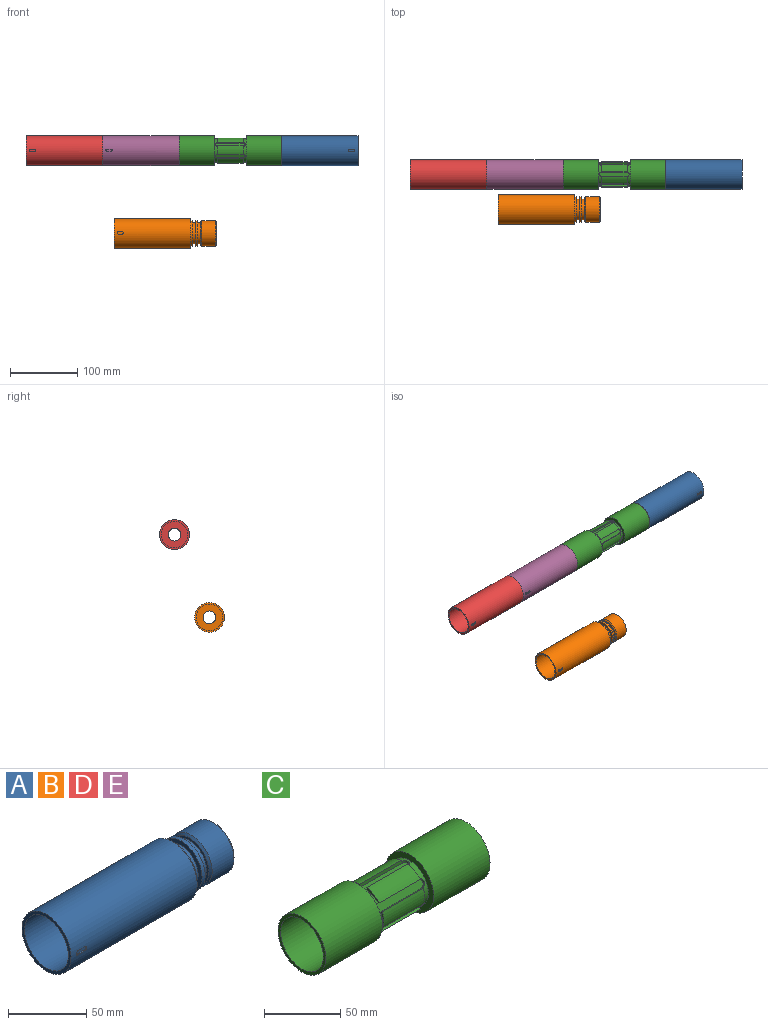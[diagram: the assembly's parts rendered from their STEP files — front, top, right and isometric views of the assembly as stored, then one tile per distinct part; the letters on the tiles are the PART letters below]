
ASSEMBLY  parts=5 mates=4
PART A: 23 faces, bbox 152.4x44.5x44.5 mm
  f0: cylinder r=19.05mm len=38.1mm, axis (1,0,0), area 2371.4mm2, adj f21,f22
  f1: cylinder r=22.23mm len=114.3mm, axis (1,0,0), area 15933.2mm2, adj f2,f8,f9,f10,f11,f12
  f2: plane 44.45x44.45mm, normal (-1,0,0), area 314.7mm2, adj f1,f3
  f3: cylinder r=19.84mm len=44.45mm, axis (1,0,0), area 5542.1mm2, adj f2,f4
  f4: plane 39.69x39.69mm, normal (-1,0,0), area 952.1mm2, adj f3,f5
  f5: cylinder r=9.53mm len=107.95mm, axis (1,0,0), area 6460.5mm2, adj f4,f6
  f6: plane 35.05x35.05mm, normal (1,0,0), area 680mm2, adj f5,f22
  f7: cylinder r=19.05mm len=38.1mm, axis (1,0,0), area 343.5mm2, adj f8,f18
  f8: plane 44.45x44.45mm, normal (1,0,0), area 411.7mm2, adj f1,f7
  f9: plane 6.35x0.96mm, normal (0,0,-1), area 6.1mm2, adj f1,f10,f12,f13
  f10: cylinder r=1.59mm len=3.18mm, axis (0,-1,0), area 4.9mm2, adj f1,f9,f11,f13
  f11: plane 6.35x0.96mm, normal (0,0,1), area 6.1mm2, adj f1,f10,f12,f13
  f12: cylinder r=1.59mm len=3.18mm, axis (0,-1,0), area 4.9mm2, adj f1,f9,f11,f13
  f13: plane 9.53x3.18mm, normal (0,-1,0), area 28.1mm2, adj f9,f10,f11,f12
  f14: plane 38.1x38.1mm, normal (1,0,0), area 385.9mm2, adj f15,f17
  f15: cylinder r=15.49mm len=30.99mm, axis (1,0,0), area 462.4mm2, adj f14,f16
  f16: plane 35.05x35.05mm, normal (-1,0,0), area 210.8mm2, adj f15,f21
  f17: cylinder r=19.05mm len=38.1mm, axis (1,0,0), area 343.5mm2, adj f14,f20
  f18: plane 38.1x38.1mm, normal (1,0,0), area 385.9mm2, adj f7,f19
  f19: cylinder r=15.49mm len=30.99mm, axis (1,0,0), area 462.4mm2, adj f18,f20
  f20: plane 38.1x38.1mm, normal (-1,0,0), area 385.9mm2, adj f17,f19
  f21: cone r=19.05mm half-angle=45deg, axis (1,0,0), area 247.7mm2, adj f0,f16
  f22: cone r=17.53mm half-angle=45deg, axis (-1,0,0), area 247.7mm2, adj f0,f6
PART B: same geometry as A
PART C: 61 faces, bbox 152.4x44.5x44.5 mm
  f0: plane 11.3x7.22mm, normal (1,0,0), area 17.2mm2, adj f22,f40,f45,f58
  f1: plane 11.3x7.22mm, normal (1,0,0), area 17.2mm2, adj f22,f44,f49,f57
  f2: plane 13.05x2.36mm, normal (1,0,0), area 17.2mm2, adj f22,f48,f53,f55
  f3: plane 11.3x7.22mm, normal (1,0,0), area 17.2mm2, adj f22,f33,f52,f56
  f4: plane 11.3x7.22mm, normal (1,0,0), area 17.2mm2, adj f22,f32,f37,f60
  f5: plane 13.05x2.36mm, normal (1,0,0), area 17.2mm2, adj f22,f36,f41,f59
  f6: plane 11.3x7.22mm, normal (-1,0,0), area 17.2mm2, adj f24,f40,f45,f58
  f7: plane 11.3x7.22mm, normal (-1,0,0), area 17.2mm2, adj f24,f44,f49,f57
  f8: plane 13.05x2.36mm, normal (-1,0,0), area 17.2mm2, adj f24,f48,f53,f55
  f9: plane 11.3x7.22mm, normal (-1,0,0), area 17.2mm2, adj f24,f33,f52,f56
  f10: plane 11.3x7.22mm, normal (-1,0,0), area 17.2mm2, adj f24,f32,f37,f60
  f11: plane 13.05x2.36mm, normal (-1,0,0), area 17.2mm2, adj f24,f36,f41,f59
  f12: cylinder r=22.23mm len=52.39mm, axis (1,0,0), area 7315.6mm2, adj f17,f21
  f13: cylinder r=22.23mm len=52.39mm, axis (1,0,0), area 7315.6mm2, adj f18,f23
  f14: cylinder r=12.7mm len=63.5mm, axis (1,0,0), area 5067.1mm2, adj f15,f20
  f15: plane 39.69x39.69mm, normal (1,0,0), area 730.4mm2, adj f14,f16
  f16: cylinder r=19.84mm len=44.45mm, axis (1,0,0), area 5542.1mm2, adj f15,f17
  f17: plane 44.45x44.45mm, normal (1,0,0), area 314.7mm2, adj f12,f16
  f18: plane 44.45x44.45mm, normal (-1,0,0), area 314.7mm2, adj f13,f19
  f19: cylinder r=19.84mm len=44.45mm, axis (1,0,0), area 5542.1mm2, adj f18,f20
  f20: plane 39.69x39.69mm, normal (-1,0,0), area 730.4mm2, adj f14,f19
  f21: plane 44.45x44.45mm, normal (-1,0,0), area 593.8mm2, adj f12,f22
  f22: cylinder r=17.46mm len=34.93mm, axis (1,0,0), area 427.1mm2, adj f0,f1,f2,f3,f4,f5,f21,f31
  f23: plane 44.45x44.45mm, normal (1,0,0), area 593.8mm2, adj f13,f24
  f24: cylinder r=17.46mm len=34.93mm, axis (1,0,0), area 427.1mm2, adj f6,f7,f8,f9,f10,f11,f23,f34
  f25: plane 44.45x6.35mm, normal (0,0,1), area 273.6mm2, adj f43,f44,f45,f46
  f26: plane 44.45x5.5mm, normal (0,0.87,0.5), area 273.6mm2, adj f47,f48,f49,f50
  f27: plane 44.45x5.5mm, normal (0,0.87,-0.5), area 273.6mm2, adj f51,f52,f53,f54
  f28: plane 44.45x6.35mm, normal (0,0,-1), area 273.6mm2, adj f31,f32,f33,f34
  f29: plane 44.45x5.5mm, normal (0,-0.87,-0.5), area 273.6mm2, adj f35,f36,f37,f38
  f30: plane 44.45x5.5mm, normal (0,-0.87,0.5), area 273.6mm2, adj f39,f40,f41,f42
  f31: cylinder r=3.17mm len=6.35mm, axis (0,0,-1), area 14.4mm2, adj f22,f28,f32,f33
  f32: plane 38.1x2.68mm, normal (0,1,0), area 102mm2, adj f4,f10,f28,f31,f34,f60
  f33: plane 38.1x2.68mm, normal (0,-1,0), area 102mm2, adj f3,f9,f28,f31,f34,f56
  f34: cylinder r=3.17mm len=6.35mm, axis (0,0,-1), area 14.4mm2, adj f24,f28,f32,f33
  f35: cylinder r=3.17mm len=6.29mm, axis (0,-0.87,-0.5), area 14.4mm2, adj f22,f29,f36,f37
  f36: plane 38.1x2.32mm, normal (0,0.5,-0.87), area 102mm2, adj f5,f11,f29,f35,f38,f59
  f37: plane 38.1x2.32mm, normal (0,-0.5,0.87), area 102mm2, adj f4,f10,f29,f35,f38,f60
  f38: cylinder r=3.17mm len=6.29mm, axis (0,-0.87,-0.5), area 14.4mm2, adj f24,f29,f36,f37
  f39: cylinder r=3.17mm len=6.29mm, axis (0,-0.87,0.5), area 14.4mm2, adj f22,f30,f40,f41
  f40: plane 38.1x2.32mm, normal (0,-0.5,-0.87), area 102mm2, adj f0,f6,f30,f39,f42,f58
  f41: plane 38.1x2.32mm, normal (0,0.5,0.87), area 102mm2, adj f5,f11,f30,f39,f42,f59
  f42: cylinder r=3.17mm len=6.29mm, axis (0,-0.87,0.5), area 14.4mm2, adj f24,f30,f40,f41
  f43: cylinder r=3.17mm len=6.35mm, axis (0,0,1), area 14.4mm2, adj f22,f25,f44,f45
  f44: plane 38.1x2.68mm, normal (0,-1,0), area 102mm2, adj f1,f7,f25,f43,f46,f57
  f45: plane 38.1x2.68mm, normal (0,1,0), area 102mm2, adj f0,f6,f25,f43,f46,f58
  f46: cylinder r=3.17mm len=6.35mm, axis (0,0,1), area 14.4mm2, adj f24,f25,f44,f45
  f47: cylinder r=3.17mm len=6.29mm, axis (0,0.87,0.5), area 14.4mm2, adj f22,f26,f48,f49
  f48: plane 38.1x2.32mm, normal (0,-0.5,0.87), area 102mm2, adj f2,f8,f26,f47,f50,f55
  f49: plane 38.1x2.32mm, normal (0,0.5,-0.87), area 102mm2, adj f1,f7,f26,f47,f50,f57
  f50: cylinder r=3.17mm len=6.29mm, axis (0,0.87,0.5), area 14.4mm2, adj f24,f26,f48,f49
  f51: cylinder r=3.17mm len=6.29mm, axis (0,0.87,-0.5), area 14.4mm2, adj f22,f27,f52,f53
  f52: plane 38.1x2.32mm, normal (0,0.5,0.87), area 102mm2, adj f3,f9,f27,f51,f54,f56
  f53: plane 38.1x2.32mm, normal (0,-0.5,-0.87), area 102mm2, adj f2,f8,f27,f51,f54,f55
  f54: cylinder r=3.17mm len=6.29mm, axis (0,0.87,-0.5), area 14.4mm2, adj f24,f27,f52,f53
  f55: cylinder r=18.82mm len=38.1mm, axis (1,0,0), area 507.9mm2, adj f2,f8,f48,f53
  f56: cylinder r=18.82mm len=38.1mm, axis (1,0,0), area 507.9mm2, adj f3,f9,f33,f52
  f57: cylinder r=18.82mm len=38.1mm, axis (1,0,0), area 507.9mm2, adj f1,f7,f44,f49
  f58: cylinder r=18.82mm len=38.1mm, axis (1,0,0), area 507.9mm2, adj f0,f6,f40,f45
  f59: cylinder r=18.82mm len=38.1mm, axis (1,0,0), area 507.9mm2, adj f5,f11,f36,f41
  f60: cylinder r=18.82mm len=38.1mm, axis (1,0,0), area 507.9mm2, adj f4,f10,f32,f37
PART D: same geometry as A
PART E: same geometry as A
PLACE A rot(axis=(0,-1,0.01),180deg) t=(307.42,-16.9,19.12)mm
PLACE B rot(axis=(-1,0,0),1.5deg) t=(-56.49,-69.03,-104.32)mm
PLACE C rot(axis=(-1,0,0),1.5deg) t=(116.92,-16.9,19.12)mm fixed
PLACE D rot(axis=(-1,0,0),1.5deg) t=(-187.88,-16.9,19.12)mm
PLACE E rot(axis=(-1,0,0),1.5deg) t=(-73.58,-16.9,19.12)mm
MATE fastened E.f0 <-> C.f12  axis (1,0,0) through (40.72,-16.9,19.12)mm
MATE parallel A.f9 <-> E.f11  axis (0,0.03,1) through (297.9,-38.63,18.11)mm
MATE fastened E.f0 <-> D.f0  axis (1,0,0) through (-73.58,-16.9,19.12)mm
MATE revolute C.f12 <-> A.f0  axis (1,0,0) through (193.12,-16.9,19.12)mm
